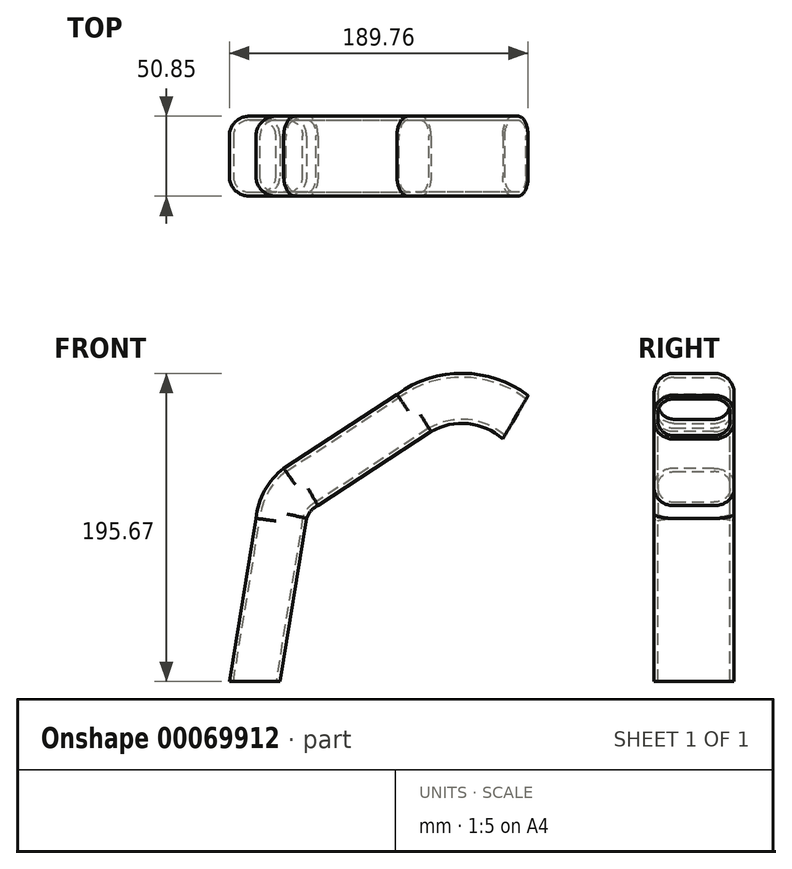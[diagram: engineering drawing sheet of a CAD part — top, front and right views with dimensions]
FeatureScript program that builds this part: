
annotation { "Feature Type Name" : "Feature", "Feature Type Description" : "" }
export const myFeature = defineFeature(function(context is Context, id is Id, definition is map)
    precondition{}
    {
        {
            var Q0;
            Q0=qCreatedBy(makeId("Top.planeOp"),FACE);
            var sketch = newSketch(context, id + "F0", { "sketchPlane" : qUnion([Q0])});
            skLineSegment(sketch, "E0.bottom", {"start": v(-61.12, 32.78) * mm, "end": v(-28.96, 32.78) * mm});
            skLineSegment(sketch, "E0.top", {"start": v(-61.12, -18.07) * mm, "end": v(-28.96, -18.07) * mm});
            skLineSegment(sketch, "E0.left", {"start": v(-61.12, 32.78) * mm, "end": v(-61.12, -18.07) * mm});
            skLineSegment(sketch, "E0.right", {"start": v(-28.96, 32.78) * mm, "end": v(-28.96, -18.07) * mm});
            skSolve(sketch);
        }
        {
            var Q0;
            Q0=qCreatedBy(makeId("Front.planeOp"),FACE);
            var sketch = newSketch(context, id + "F1", { "sketchPlane" : qUnion([Q0])});
            skLineSegment(sketch, "E1", {"start": v(-41.28, 0) * mm, "end": v(-24.33, 103.51) * mm});
            skLineSegment(sketch, "E2", {"start": v(-13.18, 120.66) * mm, "end": v(58.7, 167.71) * mm});
            skLineSegment(sketch, "E3", {"start": v(118.62, 164.58) * mm, "end": v(118.7, 164.5) * mm});
            skLineSegment(sketch, "E4", {"start": v(134.83, 109.86) * mm, "end": v(106.36, 20.52) * mm});
            skLineSegment(sketch, "E5", {"start": v(97.43, 3.97) * mm, "end": v(47.07, -58.21) * mm});
            skPoint(sketch, "E6.visualSharp", {"position": v(103.45, 11.4) * mm});
            skArc(sketch, "E6.filletArc", {"start": v(97.43, 3.97) * mm, "mid": v(102.67, 11.83) * mm, "end": v(106.36, 20.52) * mm});
            skPoint(sketch, "E7.visualSharp", {"position": v(145.3, 142.72) * mm});
            skArc(sketch, "E7.filletArc", {"start": v(134.83, 109.86) * mm, "mid": v(135.14, 139.7) * mm, "end": v(118.62, 164.58) * mm});
            skPoint(sketch, "E8.visualSharp", {"position": v(89.88, 188.13) * mm});
            skArc(sketch, "E8.filletArc", {"start": v(118.7, 164.5) * mm, "mid": v(89.22, 175.94) * mm, "end": v(58.7, 167.71) * mm});
            skPoint(sketch, "E9.visualSharp", {"position": v(-22.53, 114.54) * mm});
            skArc(sketch, "E9.filletArc", {"start": v(-13.18, 120.66) * mm, "mid": v(-20.56, 113.26) * mm, "end": v(-24.33, 103.51) * mm});
            skSolve(sketch);
        }
        {
            var Q0;
            Q0=makeQuery(id+"F0.imprint","IMPRINT",FACE,{"disambiguationData":[TD([[makeQuery(id+"F0.imprint","IMPRINT",EDGE,{"derivedFrom":sQuery(id+"F0.wireOp",EDGE,"E0.bottom")}),-1.0]])]});
            var Q1;
            Q1=sQuery(id+"F1.wireOp",EDGE,"E1");
            var Q2;
            Q2=sQuery(id+"F1.wireOp",EDGE,"E9.filletArc");
            var Q3;
            Q3=sQuery(id+"F1.wireOp",EDGE,"E2");
            var Q4;
            Q4=sQuery(id+"F1.wireOp",EDGE,"E8.filletArc");
            sweep(context, id + "F2", {"profiles" : qUnion([Q0]), "path" : qUnion([Q1, Q2, Q3, Q4])});
        }
        {
            var Q0;
            Q0=makeQuery(id+"F2.opSweep","SWEPT_EDGE",EDGE,{"disambiguationData":[OSD([sQuery(id+"F0.wireOp",EDGE,"E0.bottom"),sQuery(id+"F0.wireOp",EDGE,"E0.right"),sQuery(id+"F1.wireOp",EDGE,"E8.filletArc")])]});
            var Q1;
            Q1=makeQuery(id+"F2.opSweep","SWEPT_EDGE",EDGE,{"disambiguationData":[OSD([sQuery(id+"F0.wireOp",EDGE,"E0.bottom"),sQuery(id+"F0.wireOp",EDGE,"E0.right"),sQuery(id+"F1.wireOp",EDGE,"E2")])]});
            var Q2;
            Q2=makeQuery(id+"F2.opSweep","SWEPT_EDGE",EDGE,{"disambiguationData":[OSD([sQuery(id+"F0.wireOp",EDGE,"E0.bottom"),sQuery(id+"F0.wireOp",EDGE,"E0.right"),sQuery(id+"F1.wireOp",EDGE,"E9.filletArc")])]});
            var Q3;
            Q3=makeQuery(id+"F2.opSweep","SWEPT_EDGE",EDGE,{"disambiguationData":[OSD([sQuery(id+"F0.wireOp",EDGE,"E0.bottom"),sQuery(id+"F0.wireOp",EDGE,"E0.right"),sQuery(id+"F1.wireOp",EDGE,"E1")])]});
            var Q4;
            Q4=makeQuery(id+"F2.opSweep","SWEPT_EDGE",EDGE,{"disambiguationData":[OSD([sQuery(id+"F0.wireOp",EDGE,"E0.top"),sQuery(id+"F0.wireOp",EDGE,"E0.right"),sQuery(id+"F1.wireOp",EDGE,"E2")])]});
            var Q5;
            Q5=makeQuery(id+"F2.opSweep","SWEPT_EDGE",EDGE,{"disambiguationData":[OSD([sQuery(id+"F0.wireOp",EDGE,"E0.top"),sQuery(id+"F0.wireOp",EDGE,"E0.right"),sQuery(id+"F1.wireOp",EDGE,"E8.filletArc")])]});
            var Q6;
            Q6=makeQuery(id+"F2.opSweep","SWEPT_EDGE",EDGE,{"disambiguationData":[OSD([sQuery(id+"F0.wireOp",EDGE,"E0.top"),sQuery(id+"F0.wireOp",EDGE,"E0.right"),sQuery(id+"F1.wireOp",EDGE,"E9.filletArc")])]});
            var Q7;
            Q7=makeQuery(id+"F2.opSweep","SWEPT_EDGE",EDGE,{"disambiguationData":[OSD([sQuery(id+"F0.wireOp",EDGE,"E0.top"),sQuery(id+"F0.wireOp",EDGE,"E0.right"),sQuery(id+"F1.wireOp",EDGE,"E1")])]});
            var Q8;
            Q8=makeQuery(id+"F2.opSweep","SWEPT_EDGE",EDGE,{"disambiguationData":[OSD([sQuery(id+"F0.wireOp",EDGE,"E0.bottom"),sQuery(id+"F0.wireOp",EDGE,"E0.left"),sQuery(id+"F1.wireOp",EDGE,"E8.filletArc")])]});
            var Q9;
            Q9=makeQuery(id+"F2.opSweep","SWEPT_EDGE",EDGE,{"disambiguationData":[OSD([sQuery(id+"F0.wireOp",EDGE,"E0.top"),sQuery(id+"F0.wireOp",EDGE,"E0.left"),sQuery(id+"F1.wireOp",EDGE,"E8.filletArc")])]});
            var Q10;
            Q10=makeQuery(id+"F2.opSweep","SWEPT_EDGE",EDGE,{"disambiguationData":[OSD([sQuery(id+"F0.wireOp",EDGE,"E0.top"),sQuery(id+"F0.wireOp",EDGE,"E0.left"),sQuery(id+"F1.wireOp",EDGE,"E2")])]});
            var Q11;
            Q11=makeQuery(id+"F2.opSweep","SWEPT_EDGE",EDGE,{"disambiguationData":[OSD([sQuery(id+"F0.wireOp",EDGE,"E0.bottom"),sQuery(id+"F0.wireOp",EDGE,"E0.left"),sQuery(id+"F1.wireOp",EDGE,"E9.filletArc")])]});
            var Q12;
            Q12=makeQuery(id+"F2.opSweep","SWEPT_EDGE",EDGE,{"disambiguationData":[OSD([sQuery(id+"F0.wireOp",EDGE,"E0.top"),sQuery(id+"F0.wireOp",EDGE,"E0.left"),sQuery(id+"F1.wireOp",EDGE,"E9.filletArc")])]});
            var Q13;
            Q13=makeQuery(id+"F2.opSweep","SWEPT_EDGE",EDGE,{"disambiguationData":[OSD([sQuery(id+"F0.wireOp",EDGE,"E0.top"),sQuery(id+"F0.wireOp",EDGE,"E0.left"),sQuery(id+"F1.wireOp",EDGE,"E1")])]});
            var Q14;
            Q14=makeQuery(id+"F2.opSweep","SWEPT_EDGE",EDGE,{"disambiguationData":[OSD([sQuery(id+"F0.wireOp",EDGE,"E0.bottom"),sQuery(id+"F0.wireOp",EDGE,"E0.left"),sQuery(id+"F1.wireOp",EDGE,"E2")])]});
            var Q15;
            Q15=makeQuery(id+"F2.opSweep","SWEPT_EDGE",EDGE,{"disambiguationData":[OSD([sQuery(id+"F0.wireOp",EDGE,"E0.bottom"),sQuery(id+"F0.wireOp",EDGE,"E0.left"),sQuery(id+"F1.wireOp",EDGE,"E1")])]});
            fillet(context, id + "F3", {"entities" : qUnion([Q0, Q1, Q2, Q3, Q4, Q5, Q6, Q7, Q8, Q9, Q10, Q11, Q12, Q13, Q14, Q15]), "radius" : 12.7 * mm, "tangentPropagation" : true, "allowEdgeOverflow" : false});
        }
        {
            var Q0;
            Q0=makeQuery(id+"F2.opSweep","CAP_FACE",FACE,{"disambiguationData":[OSD([sQuery(id+"F0.wireOp",EDGE,"E0.bottom"),sQuery(id+"F0.wireOp",EDGE,"E0.top"),sQuery(id+"F0.wireOp",EDGE,"E0.left"),sQuery(id+"F0.wireOp",EDGE,"E0.right"),sQuery(id+"F1.wireOp",VERTEX,"E8.filletArc.start")])],"isStart":false});
            var Q1;
            Q1=makeQuery(id+"F2.opSweep","CAP_FACE",FACE,{"disambiguationData":[OSD([sQuery(id+"F0.wireOp",EDGE,"E0.bottom"),sQuery(id+"F0.wireOp",EDGE,"E0.top"),sQuery(id+"F0.wireOp",EDGE,"E0.left"),sQuery(id+"F0.wireOp",EDGE,"E0.right"),sQuery(id+"F1.wireOp",VERTEX,"E1.start")])],"isStart":true});
            var Q2;
            Q2=makeQuery(id+"F2.opSweep","SWEPT_BODY",BODY,{"disambiguationData":[OSD([sQuery(id+"F0.wireOp",EDGE,"E0.bottom"),sQuery(id+"F0.wireOp",EDGE,"E0.top"),sQuery(id+"F0.wireOp",EDGE,"E0.left"),sQuery(id+"F0.wireOp",EDGE,"E0.right"),sQuery(id+"F1.wireOp",EDGE,"E8.filletArc")])]});
            shell(context, id + "F4", {"entities" : qUnion([Q0, Q1]), "parts" : qUnion([Q2]), "thickness" : 2.54 * mm});
        }
    });
